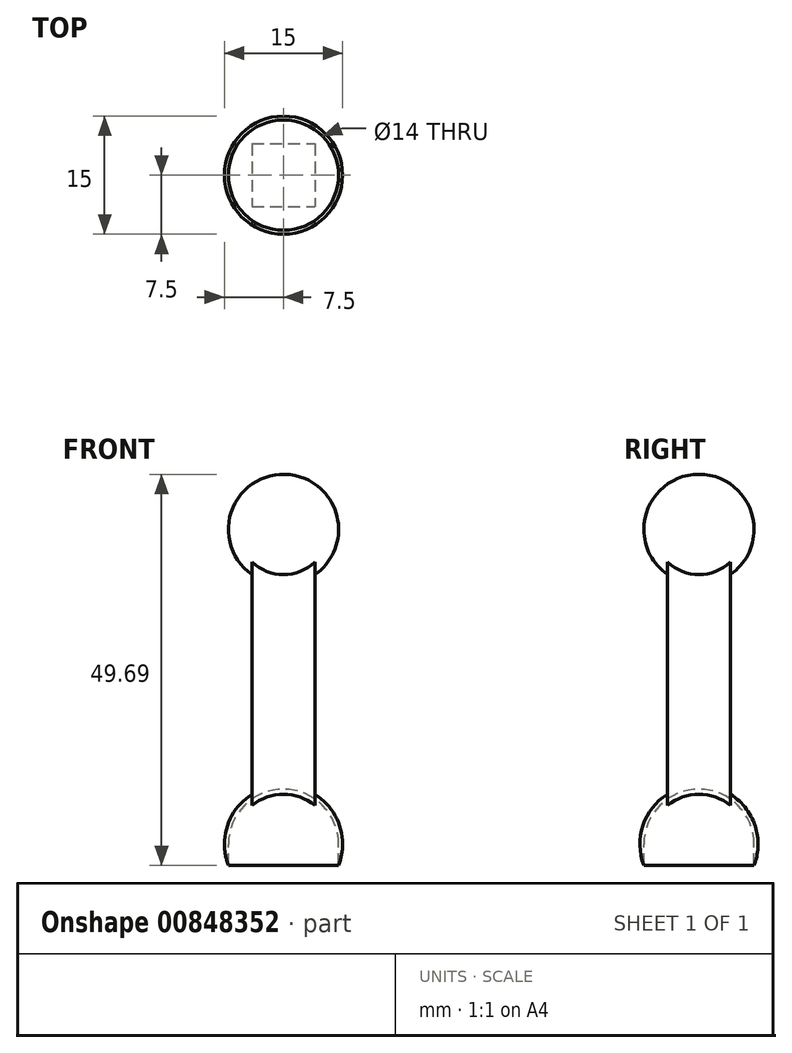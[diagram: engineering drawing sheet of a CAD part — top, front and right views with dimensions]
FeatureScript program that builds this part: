
annotation { "Feature Type Name" : "Feature", "Feature Type Description" : "" }
export const myFeature = defineFeature(function(context is Context, id is Id, definition is map)
    precondition{}
    {
        {
            var Q0;
            Q0=qCreatedBy(makeId("Top.planeOp"),FACE);
            var sketch = newSketch(context, id + "F0", { "sketchPlane" : qUnion([Q0])});
            skLineSegment(sketch, "E0", {"start": v(7.5, 0) * mm, "end": v(-7.5, 0) * mm});
            skArc(sketch, "E1", {"start": v(7.5, 0) * mm, "mid": v(0, 7.5) * mm, "end": v(-7.5, 0) * mm});
            skArc(sketch, "E2", {"start": v(7, 0) * mm, "mid": v(0, 7) * mm, "end": v(-7, 0) * mm});
            skSolve(sketch);
        }
        {
            var Q0;
            {var subQ0=sQuery(id+"F0.wireOp",EDGE,"E1");Q0=makeQuery(id+"F0.imprint","IMPRINT",FACE,{"disambiguationData":[TD([[makeQuery(id+"F0.imprint","IMPRINT",EDGE,{"derivedFrom":subQ0}),1.0]])]});}
            var Q1;
            Q1=sQuery(id+"F0.wireOp",EDGE,"E0");
            revolve(context, id + "F1", {"surfaceOperationType" : NewSurfaceOperationType.NEW, "entities" : qUnion([Q0]), "axis" : qUnion([Q1]), "revolveType" : RevolveType.FULL});
        }
        {
            var Q0;
            Q0=qCreatedBy(makeId("Top.planeOp"),FACE);
            var sketch = newSketch(context, id + "F2", { "sketchPlane" : qUnion([Q0])});
            skLineSegment(sketch, "E3.bottom", {"start": v(-4, 4) * mm, "end": v(4, 4) * mm});
            skLineSegment(sketch, "E3.top", {"start": v(-4, -4) * mm, "end": v(4, -4) * mm});
            skLineSegment(sketch, "E3.left", {"start": v(-4, 4) * mm, "end": v(-4, -4) * mm});
            skLineSegment(sketch, "E3.right", {"start": v(4, 4) * mm, "end": v(4, -4) * mm});
            skPoint(sketch, "E3.middle", {"position": v(0, 0) * mm});
            skSolve(sketch);
        }
        {
            var Q0;
            Q0 = qSketchRegion(id + "F2", true);
            extrude(context, id + "F3", {"entities" : qUnion([Q0]), "operationType" : NewBodyOperationType.ADD, "depth" : 40 * mm, "offsetDistance" : 25 * mm});
        }
        {
            var Q0;
            Q0=qCreatedBy(makeId("Top.planeOp"),FACE);
            var sketch = newSketch(context, id + "F4", { "sketchPlane" : qUnion([Q0])});
            skCircle(sketch, "E4", {"center": v(0, 0) * mm, "radius": 7 * mm});
            skSolve(sketch);
        }
        {
            var Q0;
            Q0 = qSketchRegion(id + "F4", true);
            extrude(context, id + "F5", {"entities" : qUnion([Q0]), "operationType" : NewBodyOperationType.REMOVE, "oppositeDirection" : true, "depth" : 7.5 * mm, "offsetDistance" : 25 * mm});
        }
        {
            var Q0;
            Q0=makeQuery(id+"F3.opExtrude","CAP_FACE",FACE,{"disambiguationData":[OSD([sQuery(id+"F2.wireOp",EDGE,"E3.bottom"),sQuery(id+"F2.wireOp",EDGE,"E3.top"),sQuery(id+"F2.wireOp",EDGE,"E3.left"),sQuery(id+"F2.wireOp",EDGE,"E3.right")])],"isStart":true});
            var sketch = newSketch(context, id + "F6", { "sketchPlane" : qUnion([Q0])});
            skLineSegment(sketch, "E5", {"start": v(0, 7) * mm, "end": v(0, -7) * mm});
            skArc(sketch, "E6", {"start": v(0, -7) * mm, "mid": v(7, 0) * mm, "end": v(0, 7) * mm});
            skSolve(sketch);
        }
        {
            var Q0;
            {var subQ0=sQuery(id+"F6.wireOp",EDGE,"E6");var subQ1=sQuery(id+"F6.wireOp",EDGE,"E5");var subQ2=makeQuery(id+"F6.imprint","INTERSECT",VERTEX,{"disambiguationData":[OD(0.0)],"derivedFrom":[subQ1,subQ0]});Q0=makeQuery(id+"F6.imprint","IMPRINT",FACE,{"disambiguationData":[TD([[makeQuery(id+"F6.imprint","IMPRINT",EDGE,{"disambiguationData":[TD([[subQ2,-1.0]])],"derivedFrom":subQ1}),1.0]])]});}
            var Q1;
            {var subQ3=makeQuery(id+"F3.opExtrude","CAP_EDGE",EDGE,{"disambiguationData":[OSD([sQuery(id+"F2.wireOp",EDGE,"E3.right")])],"isStart":true});Q1=makeQuery(id+"F6.imprint","IMPRINT",FACE,{"disambiguationData":[TD([[makeQuery(id+"F6.imprint","IMPRINT",EDGE,{"derivedFrom":subQ3}),1.0]])]});}
            var Q2;
            {var subQ1=makeQuery(id+"F3.opExtrude","CAP_EDGE",EDGE,{"disambiguationData":[OSD([sQuery(id+"F2.wireOp",EDGE,"E3.right")])],"isStart":true});Q2=makeQuery(id+"F6.imprint","IMPRINT",FACE,{"disambiguationData":[TD([[makeQuery(id+"F6.imprint","IMPRINT",EDGE,{"derivedFrom":subQ1}),-1.0]])]});}
            var Q3;
            {var subQ0=sQuery(id+"F6.wireOp",EDGE,"E6");var subQ1=sQuery(id+"F6.wireOp",EDGE,"E5");var subQ2=makeQuery(id+"F6.imprint","INTERSECT",VERTEX,{"disambiguationData":[OD(1.0)],"derivedFrom":[subQ1,subQ0]});Q3=makeQuery(id+"F6.imprint","IMPRINT",FACE,{"disambiguationData":[TD([[makeQuery(id+"F6.imprint","IMPRINT",EDGE,{"disambiguationData":[TD([[subQ2,1.0]])],"derivedFrom":subQ1}),1.0]])]});}
            var Q4;
            Q4=sQuery(id+"F6.wireOp",EDGE,"E5");
            revolve(context, id + "F7", {"operationType" : NewBodyOperationType.REMOVE, "surfaceOperationType" : NewSurfaceOperationType.NEW, "entities" : qUnion([Q0, Q1, Q2, Q3]), "axis" : qUnion([Q4]), "revolveType" : RevolveType.FULL, "oppositeDirection" : true});
        }
        {
            var Q0;
            Q0=makeQuery(id+"F3.opExtrude","CAP_FACE",FACE,{"disambiguationData":[OSD([sQuery(id+"F2.wireOp",EDGE,"E3.bottom"),sQuery(id+"F2.wireOp",EDGE,"E3.top"),sQuery(id+"F2.wireOp",EDGE,"E3.left"),sQuery(id+"F2.wireOp",EDGE,"E3.right")])],"isStart":false});
            var sketch = newSketch(context, id + "F8", { "sketchPlane" : qUnion([Q0])});
            skLineSegment(sketch, "E7", {"start": v(0, 7) * mm, "end": v(0, -7) * mm});
            skArc(sketch, "E8", {"start": v(0, -7) * mm, "mid": v(7, 0) * mm, "end": v(0, 7) * mm});
            skSolve(sketch);
        }
        {
            var Q0;
            {var subQ0=sQuery(id+"F8.wireOp",EDGE,"E8");var subQ1=sQuery(id+"F8.wireOp",EDGE,"E7");var subQ2=makeQuery(id+"F8.imprint","INTERSECT",VERTEX,{"disambiguationData":[OD(0.0)],"derivedFrom":[subQ1,subQ0]});Q0=makeQuery(id+"F8.imprint","IMPRINT",FACE,{"disambiguationData":[TD([[makeQuery(id+"F8.imprint","IMPRINT",EDGE,{"disambiguationData":[TD([[subQ2,-1.0]])],"derivedFrom":subQ1}),1.0]])]});}
            var Q1;
            {var subQ0=sQuery(id+"F8.wireOp",EDGE,"E8");var subQ1=makeQuery(id+"F3.opExtrude","CAP_EDGE",EDGE,{"disambiguationData":[OSD([sQuery(id+"F2.wireOp",EDGE,"E3.right")])],"isStart":false});var subQ2=makeQuery(id+"F8.imprint","INTERSECT",VERTEX,{"disambiguationData":[OD(0.0)],"derivedFrom":[subQ1,subQ0]});Q1=makeQuery(id+"F8.imprint","IMPRINT",FACE,{"disambiguationData":[TD([[makeQuery(id+"F8.imprint","IMPRINT",EDGE,{"disambiguationData":[TD([[subQ2,-1.0]])],"derivedFrom":subQ0}),1.0]])]});}
            var Q2;
            {var subQ5=sQuery(id+"F8.wireOp",EDGE,"E7");var subQ6=makeQuery(id+"F3.opExtrude","CAP_EDGE",EDGE,{"disambiguationData":[OSD([sQuery(id+"F2.wireOp",EDGE,"E3.bottom")])],"isStart":false});var subQ7=makeQuery(id+"F8.imprint","INTERSECT",VERTEX,{"derivedFrom":[subQ6,subQ5]});Q2=makeQuery(id+"F8.imprint","IMPRINT",FACE,{"disambiguationData":[TD([[makeQuery(id+"F8.imprint","IMPRINT",EDGE,{"disambiguationData":[TD([[subQ7,-1.0]])],"derivedFrom":subQ5}),1.0]])]});}
            var Q3;
            {var subQ0=sQuery(id+"F8.wireOp",EDGE,"E8");var subQ1=sQuery(id+"F8.wireOp",EDGE,"E7");var subQ2=makeQuery(id+"F8.imprint","INTERSECT",VERTEX,{"disambiguationData":[OD(1.0)],"derivedFrom":[subQ1,subQ0]});Q3=makeQuery(id+"F8.imprint","IMPRINT",FACE,{"disambiguationData":[TD([[makeQuery(id+"F8.imprint","IMPRINT",EDGE,{"disambiguationData":[TD([[subQ2,1.0]])],"derivedFrom":subQ1}),1.0]])]});}
            var Q4;
            Q4=sQuery(id+"F8.wireOp",EDGE,"E7");
            revolve(context, id + "F9", {"operationType" : NewBodyOperationType.ADD, "surfaceOperationType" : NewSurfaceOperationType.NEW, "entities" : qUnion([Q0, Q1, Q2, Q3]), "axis" : qUnion([Q4]), "revolveType" : RevolveType.FULL});
        }
    });
